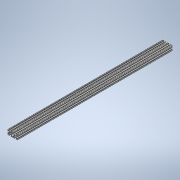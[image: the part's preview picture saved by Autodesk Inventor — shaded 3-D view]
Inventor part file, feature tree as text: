
AUTODESK INVENTOR PART (.ipt)
format: ipt  version: 2020 (Build 240168000, 168)  size: 336,896 bytes
history: native  units: in
note: dims shown in document units (in); Inventor stores cm internally (conversion verified against a paired STEP export)
features: sketch x2, extrude x1
ambient origin geometry x8: Origin, YZ Plane, XZ Plane, XY Plane, X Axis, Y Axis, Z Axis, Center Point
bodies: Solid1 (feature_tree)
feature tree (3):
  extrude  "Extrusion1"  [1 undecoded]
  sketch  "Sketch2"
  sketch  "Sketch1"  dims[d0=31.0in d1=0.0in]
note: 1 required parameter value undecoded (feature->parameter linkage not recoverable at this tier; creation-order binding heuristic only, values carry confidence <= 0.55)
